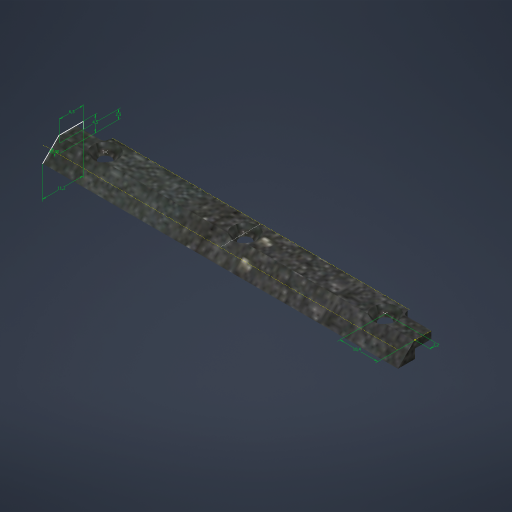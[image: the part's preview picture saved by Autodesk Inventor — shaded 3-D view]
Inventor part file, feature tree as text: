
AUTODESK INVENTOR PART (.ipt)
format: ipt  version: 2023 (Build 270158000, 158)  size: 340,992 bytes
history: native  units: mm
features: sketch x3, extrude x2, other x1, hole x1, fillet x1
ambient origin geometry x8: Origin, YZ Plane, XZ Plane, XY Plane, X Axis, Y Axis, Z Axis, Center Point
bodies: Body1 (feature_tree)
feature tree (8):
  other  "Bryła1"
  sketch  "Szkic1"
  extrude  "Wyciągnięcie proste1"  Depth=11.2mm
  extrude  "Wyciągnięcie proste2"  Depth=4.5mm
  hole  "Otwór1"  [1 undecoded]
  fillet  "Zaokrąglenie1"  Radius=2.5mm
  sketch  "Szkic2"
  sketch  "Szkic3"
note: 1 required parameter value undecoded (feature->parameter linkage not recoverable at this tier; creation-order binding heuristic only, values carry confidence <= 0.55)
